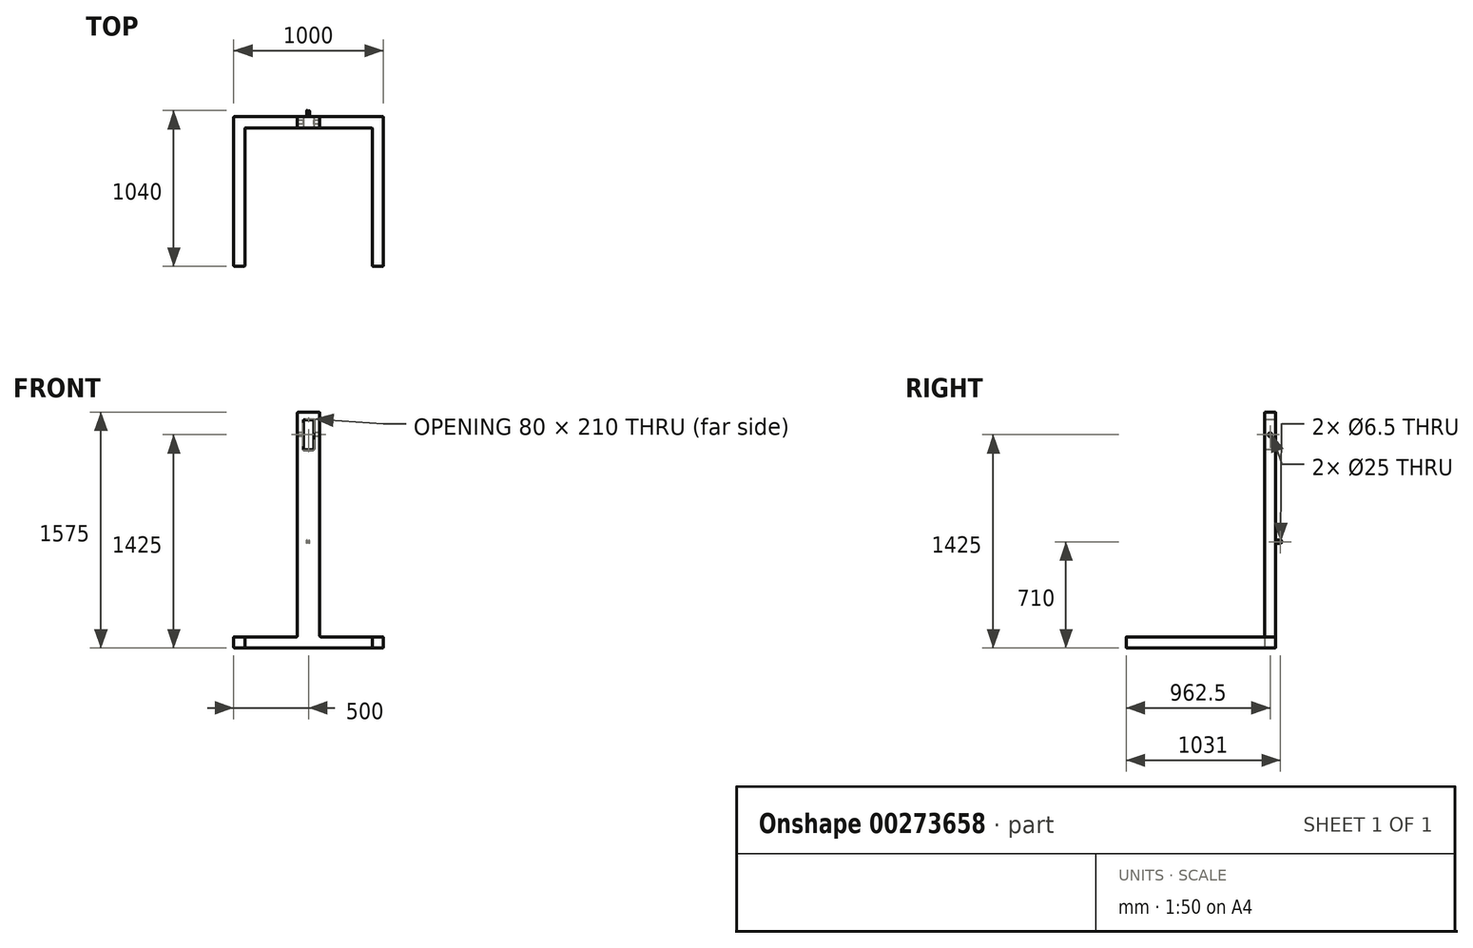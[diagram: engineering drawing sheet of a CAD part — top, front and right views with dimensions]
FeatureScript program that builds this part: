
annotation { "Feature Type Name" : "Feature", "Feature Type Description" : "" }
export const myFeature = defineFeature(function(context is Context, id is Id, definition is map)
    precondition{}
    {
        {
            var Q0;
            Q0=qCreatedBy(makeId("Top.planeOp"),FACE);
            var sketch = newSketch(context, id + "F0", { "sketchPlane" : qUnion([Q0])});
            skLineSegment(sketch, "E0.bottom", {"start": v(-500, 0) * mm, "end": v(500, 0) * mm});
            skLineSegment(sketch, "E0.top", {"start": v(-500, -1000) * mm, "end": v(-425, -1000) * mm});
            skLineSegment(sketch, "E0.left", {"start": v(-500, 0) * mm, "end": v(-500, -1000) * mm});
            skLineSegment(sketch, "E0.right", {"start": v(500, 0) * mm, "end": v(500, -1000) * mm});
            skLineSegment(sketch, "E1.0", {"start": v(-505, 5) * mm, "end": v(-505, -1000) * mm});
            skLineSegment(sketch, "E1.1", {"start": v(-505, 5) * mm, "end": v(505, 5) * mm});
            skLineSegment(sketch, "E1.2", {"start": v(505, 5) * mm, "end": v(505, -1000) * mm});
            skLineSegment(sketch, "E2.0", {"start": v(-425, -75) * mm, "end": v(-425, -1000) * mm});
            skLineSegment(sketch, "E2.1", {"start": v(-425, -75) * mm, "end": v(425, -75) * mm});
            skLineSegment(sketch, "E2.2", {"start": v(425, -75) * mm, "end": v(425, -1000) * mm});
            skLineSegment(sketch, "E3.trimOffspring", {"start": v(425, -1000) * mm, "end": v(500, -1000) * mm});
            skSolve(sketch);
        }
        {
            var Q0;
            Q0=makeQuery(id+"F0.imprint","IMPRINT",FACE,{"disambiguationData":[TD([[makeQuery(id+"F0.imprint","IMPRINT",EDGE,{"derivedFrom":sQuery(id+"F0.wireOp",EDGE,"E0.bottom")}),-1.0]])]});
            extrude(context, id + "F1", {"entities" : qUnion([Q0]), "depth" : 75 * mm});
        }
        {
            var Q0;
            Q0=makeQuery(id+"F1.opExtrude","CAP_FACE",FACE,{"disambiguationData":[OSD([sQuery(id+"F0.wireOp",EDGE,"E0.bottom"),sQuery(id+"F0.wireOp",EDGE,"E0.top"),sQuery(id+"F0.wireOp",EDGE,"E0.left"),sQuery(id+"F0.wireOp",EDGE,"E0.right"),sQuery(id+"F0.wireOp",EDGE,"E2.0"),sQuery(id+"F0.wireOp",EDGE,"E2.1"),sQuery(id+"F0.wireOp",EDGE,"E2.2"),sQuery(id+"F0.wireOp",EDGE,"E3.trimOffspring")])],"isStart":false});
            var sketch = newSketch(context, id + "F2", { "sketchPlane" : qUnion([Q0])});
            skLineSegment(sketch, "E4.bottom", {"start": v(75, -75) * mm, "end": v(-75, -75) * mm});
            skLineSegment(sketch, "E4.left", {"start": v(75, -75) * mm, "end": v(75, 0) * mm});
            skLineSegment(sketch, "E4.right", {"start": v(-75, -75) * mm, "end": v(-75, 0) * mm});
            skPoint(sketch, "E4.middle", {"position": v(0, 0) * mm});
            skLineSegment(sketch, "E5", {"start": v(-75, 0) * mm, "end": v(75, 0) * mm});
            skPoint(sketch, "E4.top.end.orphan", {"position": v(-75, 75) * mm});
            skPoint(sketch, "E6.orphan", {"position": v(75, 75) * mm});
            skSolve(sketch);
        }
        {
            var Q0;
            Q0=makeQuery(id+"F2.imprint","IMPRINT",FACE,{"disambiguationData":[TD([[makeQuery(id+"F2.imprint","IMPRINT",EDGE,{"derivedFrom":sQuery(id+"F2.wireOp",EDGE,"E4.bottom")}),1.0]])]});
            extrude(context, id + "F3", {"entities" : qUnion([Q0]), "operationType" : NewBodyOperationType.ADD, "depth" : 1500 * mm});
        }
        {
            var Q0;
            Q0=makeQuery(id+"F3.boolean.opBoolean","MERGE",FACE,{"derivedFrom":[makeQuery(id+"F1.opExtrude","SWEPT_FACE",FACE,{"disambiguationData":[OSD([sQuery(id+"F0.wireOp",EDGE,"E2.1")])]}),makeQuery(id+"F3.opExtrude","SWEPT_FACE",FACE,{"disambiguationData":[OSD([sQuery(id+"F2.wireOp",EDGE,"E4.bottom")])]})]});
            var sketch = newSketch(context, id + "F4", { "sketchPlane" : qUnion([Q0])});
            skLineSegment(sketch, "E7.bottom", {"start": v(-35, 1525) * mm, "end": v(35, 1525) * mm});
            skLineSegment(sketch, "E7.top", {"start": v(-35, 1325) * mm, "end": v(35, 1325) * mm});
            skLineSegment(sketch, "E7.left", {"start": v(-35, 1525) * mm, "end": v(-35, 1325) * mm});
            skLineSegment(sketch, "E7.right", {"start": v(35, 1525) * mm, "end": v(35, 1325) * mm});
            skSolve(sketch);
        }
        {
            var Q0;
            Q0=makeQuery(id+"F4.imprint","IMPRINT",FACE,{"disambiguationData":[TD([[makeQuery(id+"F4.imprint","IMPRINT",EDGE,{"derivedFrom":sQuery(id+"F4.wireOp",EDGE,"E7.bottom")}),-1.0]])]});
            extrude(context, id + "F5", {"entities" : qUnion([Q0]), "operationType" : NewBodyOperationType.REMOVE, "endBound" : BoundingType.THROUGH_ALL, "oppositeDirection" : true, "depth" : 25 * mm});
        }
        {
            var Q0;
            Q0=makeQuery(id+"F3.boolean.opBoolean","MERGE",FACE,{"derivedFrom":[makeQuery(id+"F1.opExtrude","SWEPT_FACE",FACE,{"disambiguationData":[OSD([sQuery(id+"F0.wireOp",EDGE,"E0.bottom")])]}),makeQuery(id+"F3.opExtrude","SWEPT_FACE",FACE,{"disambiguationData":[OSD([sQuery(id+"F2.wireOp",EDGE,"E5")])]})]});
            var sketch = newSketch(context, id + "F6", { "sketchPlane" : qUnion([Q0])});
            skLineSegment(sketch, "E8.bottom", {"start": v(-7.5, 700) * mm, "end": v(-1.5, 700) * mm});
            skLineSegment(sketch, "E8.top", {"start": v(-7.5, 720) * mm, "end": v(-1.5, 720) * mm});
            skLineSegment(sketch, "E8.left", {"start": v(-7.5, 700) * mm, "end": v(-7.5, 720) * mm});
            skLineSegment(sketch, "E8.right", {"start": v(-1.5, 700) * mm, "end": v(-1.5, 720) * mm});
            skLineSegment(sketch, "E9.1.0.0", {"start": v(7.5, 700) * mm, "end": v(13.5, 700) * mm});
            skLineSegment(sketch, "E9.1.0.1", {"start": v(7.5, 720) * mm, "end": v(13.5, 720) * mm});
            skLineSegment(sketch, "E9.1.0.2", {"start": v(7.5, 700) * mm, "end": v(7.5, 720) * mm});
            skLineSegment(sketch, "E9.1.0.3", {"start": v(13.5, 700) * mm, "end": v(13.5, 720) * mm});
            skLineSegment(sketch, "E9.direction1", {"start": v(-7.5, 700) * mm, "end": v(7.5, 700) * mm, "construction": true});
            skSolve(sketch);
        }
        {
            var Q0;
            Q0=makeQuery(id+"F6.imprint","IMPRINT",FACE,{"disambiguationData":[TD([[makeQuery(id+"F6.imprint","IMPRINT",EDGE,{"derivedFrom":sQuery(id+"F6.wireOp",EDGE,"E8.bottom")}),1.0]])]});
            var Q1;
            Q1=makeQuery(id+"F6.imprint","IMPRINT",FACE,{"disambiguationData":[TD([[makeQuery(id+"F6.imprint","IMPRINT",EDGE,{"derivedFrom":sQuery(id+"F6.wireOp",EDGE,"E9.1.0.0")}),1.0]])]});
            extrude(context, id + "F7", {"entities" : qUnion([Q0, Q1]), "operationType" : NewBodyOperationType.ADD, "depth" : 40 * mm});
        }
        {
            var Q0;
            Q0=makeQuery(id+"F7.opExtrude","CAP_EDGE",EDGE,{"disambiguationData":[OSD([sQuery(id+"F6.wireOp",EDGE,"E8.top")])],"isStart":false});
            var Q1;
            Q1=makeQuery(id+"F7.opExtrude","CAP_EDGE",EDGE,{"disambiguationData":[OSD([sQuery(id+"F6.wireOp",EDGE,"E8.bottom")])],"isStart":false});
            var Q2;
            Q2=makeQuery(id+"F7.opExtrude","CAP_EDGE",EDGE,{"disambiguationData":[OSD([sQuery(id+"F6.wireOp",EDGE,"E9.1.0.1")])],"isStart":false});
            var Q3;
            Q3=makeQuery(id+"F7.opExtrude","CAP_EDGE",EDGE,{"disambiguationData":[OSD([sQuery(id+"F6.wireOp",EDGE,"E9.1.0.0")])],"isStart":false});
            fillet(context, id + "F8", {"entities" : qUnion([Q0, Q1, Q2, Q3]), "radius" : 10 * mm, "tangentPropagation" : true, "allowEdgeOverflow" : false});
        }
        {
            var Q0;
            Q0=makeQuery(id+"F7.opExtrude","SWEPT_FACE",FACE,{"disambiguationData":[OSD([sQuery(id+"F6.wireOp",EDGE,"E8.left")])]});
            var sketch = newSketch(context, id + "F9", { "sketchPlane" : qUnion([Q0])});
            skCircle(sketch, "E10", {"center": v(31, 710) * mm, "radius": 3.25 * mm});
            skSolve(sketch);
        }
        {
            var Q0;
            Q0 = qSketchRegion(id + "F9", true);
            extrude(context, id + "F10", {"entities" : qUnion([Q0]), "operationType" : NewBodyOperationType.REMOVE, "endBound" : BoundingType.THROUGH_ALL, "oppositeDirection" : true, "depth" : 25 * mm});
        }
        {
            var Q0;
            Q0=makeQuery(id+"F3.boolean.opBoolean","MERGE",FACE,{"derivedFrom":[makeQuery(id+"F1.opExtrude","SWEPT_FACE",FACE,{"disambiguationData":[OSD([sQuery(id+"F0.wireOp",EDGE,"E2.1")])]}),makeQuery(id+"F3.opExtrude","SWEPT_FACE",FACE,{"disambiguationData":[OSD([sQuery(id+"F2.wireOp",EDGE,"E4.bottom")])]})]});
            var Q1;
            {var subQ0=sQuery(id+"F0.wireOp",EDGE,"E2.0");var subQ1=sQuery(id+"F0.wireOp",EDGE,"E0.left");var subQ2=sQuery(id+"F0.wireOp",EDGE,"E0.top");var subQ3=sQuery(id+"F0.wireOp",EDGE,"E0.bottom");var subQ4=sQuery(id+"F0.wireOp",EDGE,"E2.1");Q1=makeQuery(id+"F3.boolean.opBoolean","SPLIT",FACE,{"disambiguationData":[TD([makeQuery(id+"F1.opExtrude","SWEPT_FACE",FACE,{"disambiguationData":[OSD([subQ2])]})])],"derivedFrom":makeQuery(id+"F1.opExtrude","CAP_FACE",FACE,{"disambiguationData":[OSD([subQ3,subQ2,subQ1,sQuery(id+"F0.wireOp",EDGE,"E0.right"),subQ0,subQ4,sQuery(id+"F0.wireOp",EDGE,"E2.2"),sQuery(id+"F0.wireOp",EDGE,"E3.trimOffspring")])],"isStart":false})});}
            var Q2;
            {var subQ0=sQuery(id+"F0.wireOp",EDGE,"E2.2");var subQ1=sQuery(id+"F0.wireOp",EDGE,"E2.1");var subQ2=sQuery(id+"F0.wireOp",EDGE,"E0.right");var subQ3=sQuery(id+"F0.wireOp",EDGE,"E0.bottom");var subQ4=sQuery(id+"F0.wireOp",EDGE,"E3.trimOffspring");Q2=makeQuery(id+"F3.boolean.opBoolean","SPLIT",FACE,{"disambiguationData":[TD([makeQuery(id+"F1.opExtrude","SWEPT_FACE",FACE,{"disambiguationData":[OSD([subQ2])]})])],"derivedFrom":makeQuery(id+"F1.opExtrude","CAP_FACE",FACE,{"disambiguationData":[OSD([subQ3,sQuery(id+"F0.wireOp",EDGE,"E0.top"),sQuery(id+"F0.wireOp",EDGE,"E0.left"),subQ2,sQuery(id+"F0.wireOp",EDGE,"E2.0"),subQ1,subQ0,subQ4])],"isStart":false})});}
            var Q3;
            Q3=makeQuery(id+"F1.opExtrude","SWEPT_FACE",FACE,{"disambiguationData":[OSD([sQuery(id+"F0.wireOp",EDGE,"E0.top")])]});
            var Q4;
            Q4=makeQuery(id+"F1.opExtrude","SWEPT_FACE",FACE,{"disambiguationData":[OSD([sQuery(id+"F0.wireOp",EDGE,"E3.trimOffspring")])]});
            var Q5;
            Q5=makeQuery(id+"F1.opExtrude","SWEPT_FACE",FACE,{"disambiguationData":[OSD([sQuery(id+"F0.wireOp",EDGE,"E0.left")])]});
            var Q6;
            Q6=makeQuery(id+"F1.opExtrude","SWEPT_EDGE",EDGE,{"disambiguationData":[OSD([sQuery(id+"F0.wireOp",EDGE,"E0.top"),sQuery(id+"F0.wireOp",EDGE,"E0.left")])]});
            var Q7;
            Q7=makeQuery(id+"F3.opExtrude","SWEPT_EDGE",EDGE,{"disambiguationData":[OSD([sQuery(id+"F0.wireOp",EDGE,"E2.1"),sQuery(id+"F2.wireOp",EDGE,"E4.bottom"),sQuery(id+"F2.wireOp",EDGE,"E4.left")])]});
            var Q8;
            Q8=makeQuery(id+"F1.opExtrude","SWEPT_EDGE",EDGE,{"disambiguationData":[OSD([sQuery(id+"F0.wireOp",EDGE,"E2.2"),sQuery(id+"F0.wireOp",EDGE,"E3.trimOffspring")])]});
            var Q9;
            Q9=makeQuery(id+"F3.opExtrude","SWEPT_EDGE",EDGE,{"disambiguationData":[OSD([sQuery(id+"F0.wireOp",EDGE,"E2.1"),sQuery(id+"F2.wireOp",EDGE,"E4.bottom"),sQuery(id+"F2.wireOp",EDGE,"E4.right")])]});
            var Q10;
            Q10=makeQuery(id+"F5.boolean.opBoolean","COPY",EDGE,{"derivedFrom":makeQuery(id+"F5.opExtrude","CAP_EDGE",EDGE,{"disambiguationData":[OSD([sQuery(id+"F4.wireOp",EDGE,"E7.right")])],"isStart":true})});
            var Q11;
            Q11=makeQuery(id+"F1.opExtrude","SWEPT_EDGE",EDGE,{"disambiguationData":[OSD([sQuery(id+"F0.wireOp",EDGE,"E0.top"),sQuery(id+"F0.wireOp",EDGE,"E2.0")])]});
            var Q12;
            Q12=makeQuery(id+"F1.opExtrude","SWEPT_EDGE",EDGE,{"disambiguationData":[OSD([sQuery(id+"F0.wireOp",EDGE,"E2.1"),sQuery(id+"F0.wireOp",EDGE,"E2.2")])]});
            var Q13;
            Q13=makeQuery(id+"F3.opExtrude","SWEPT_EDGE",EDGE,{"disambiguationData":[OSD([sQuery(id+"F0.wireOp",EDGE,"E0.bottom"),sQuery(id+"F2.wireOp",EDGE,"E4.left"),sQuery(id+"F2.wireOp",EDGE,"E5")])]});
            var Q14;
            Q14=makeQuery(id+"F1.opExtrude","SWEPT_EDGE",EDGE,{"disambiguationData":[OSD([sQuery(id+"F0.wireOp",EDGE,"E2.0"),sQuery(id+"F0.wireOp",EDGE,"E2.1")])]});
            var Q15;
            Q15=makeQuery(id+"F1.opExtrude","SWEPT_EDGE",EDGE,{"disambiguationData":[OSD([sQuery(id+"F0.wireOp",EDGE,"E0.bottom"),sQuery(id+"F0.wireOp",EDGE,"E0.left")])]});
            var Q16;
            Q16=makeQuery(id+"F1.opExtrude","CAP_EDGE",EDGE,{"disambiguationData":[OSD([sQuery(id+"F0.wireOp",EDGE,"E0.right")])],"isStart":false});
            var Q17;
            Q17=makeQuery(id+"F1.opExtrude","CAP_EDGE",EDGE,{"disambiguationData":[OSD([sQuery(id+"F0.wireOp",EDGE,"E0.right")])],"isStart":true});
            var Q18;
            Q18=makeQuery(id+"F1.opExtrude","CAP_EDGE",EDGE,{"disambiguationData":[OSD([sQuery(id+"F0.wireOp",EDGE,"E0.left")])],"isStart":false});
            var Q19;
            Q19=makeQuery(id+"F1.opExtrude","CAP_EDGE",EDGE,{"disambiguationData":[OSD([sQuery(id+"F0.wireOp",EDGE,"E0.top")])],"isStart":true});
            var Q20;
            Q20=makeQuery(id+"F1.opExtrude","CAP_EDGE",EDGE,{"disambiguationData":[OSD([sQuery(id+"F0.wireOp",EDGE,"E0.left")])],"isStart":true});
            var Q21;
            Q21=makeQuery(id+"F1.opExtrude","CAP_EDGE",EDGE,{"disambiguationData":[OSD([sQuery(id+"F0.wireOp",EDGE,"E2.0")])],"isStart":true});
            var Q22;
            Q22=makeQuery(id+"F1.opExtrude","CAP_EDGE",EDGE,{"disambiguationData":[OSD([sQuery(id+"F0.wireOp",EDGE,"E2.0")])],"isStart":false});
            var Q23;
            Q23=makeQuery(id+"F1.opExtrude","CAP_EDGE",EDGE,{"disambiguationData":[OSD([sQuery(id+"F0.wireOp",EDGE,"E2.2")])],"isStart":true});
            var Q24;
            Q24=makeQuery(id+"F1.opExtrude","CAP_EDGE",EDGE,{"disambiguationData":[OSD([sQuery(id+"F0.wireOp",EDGE,"E2.2")])],"isStart":false});
            var Q25;
            Q25=makeQuery(id+"F3.opExtrude","SWEPT_EDGE",EDGE,{"disambiguationData":[OSD([sQuery(id+"F0.wireOp",EDGE,"E0.bottom"),sQuery(id+"F2.wireOp",EDGE,"E4.right"),sQuery(id+"F2.wireOp",EDGE,"E5")])]});
            var Q26;
            Q26=makeQuery(id+"F3.opExtrude","CAP_EDGE",EDGE,{"disambiguationData":[OSD([sQuery(id+"F2.wireOp",EDGE,"E4.bottom")])],"isStart":false});
            var Q27;
            Q27=makeQuery(id+"F3.opExtrude","CAP_EDGE",EDGE,{"disambiguationData":[OSD([sQuery(id+"F2.wireOp",EDGE,"E4.right")])],"isStart":false});
            var Q28;
            Q28=makeQuery(id+"F3.opExtrude","CAP_EDGE",EDGE,{"disambiguationData":[OSD([sQuery(id+"F2.wireOp",EDGE,"E4.right")])],"isStart":true});
            var Q29;
            {var subQ0=sQuery(id+"F0.wireOp",EDGE,"E2.1");var subQ1=sQuery(id+"F0.wireOp",EDGE,"E2.2");Q29=makeQuery(id+"F3.boolean.opBoolean","SPLIT",EDGE,{"disambiguationData":[TD([makeQuery(id+"F1.opExtrude","SWEPT_FACE",FACE,{"disambiguationData":[OSD([subQ1])]})])],"derivedFrom":makeQuery(id+"F1.opExtrude","CAP_EDGE",EDGE,{"disambiguationData":[OSD([subQ0])],"isStart":false})});}
            var Q30;
            Q30=makeQuery(id+"F5.boolean.opBoolean","COPY",EDGE,{"derivedFrom":makeQuery(id+"F5.opExtrude","SWEPT_EDGE",EDGE,{"disambiguationData":[OSD([sQuery(id+"F4.wireOp",EDGE,"E7.top"),sQuery(id+"F4.wireOp",EDGE,"E7.left")])]})});
            var Q31;
            Q31=makeQuery(id+"F7.opExtrude","CAP_EDGE",EDGE,{"disambiguationData":[OSD([sQuery(id+"F6.wireOp",EDGE,"E8.top")])],"isStart":true});
            var Q32;
            Q32=makeQuery(id+"F8.opFillet","BLEND_EDGE",EDGE,{"blendedFrom":[makeQuery(id+"F7.opExtrude","CAP_EDGE",EDGE,{"disambiguationData":[OSD([sQuery(id+"F6.wireOp",EDGE,"E8.top")])],"isStart":false}),makeQuery(id+"F7.opExtrude","SWEPT_FACE",FACE,{"disambiguationData":[OSD([sQuery(id+"F6.wireOp",EDGE,"E8.right")])]})],"blendedInto":[makeQuery(id+"F7.opExtrude","SWEPT_FACE",FACE,{"disambiguationData":[OSD([sQuery(id+"F6.wireOp",EDGE,"E8.right")])]})]});
            var Q33;
            Q33=makeQuery(id+"F7.opExtrude","CAP_EDGE",EDGE,{"disambiguationData":[OSD([sQuery(id+"F6.wireOp",EDGE,"E8.bottom")])],"isStart":true});
            var Q34;
            Q34=makeQuery(id+"F7.opExtrude","CAP_EDGE",EDGE,{"disambiguationData":[OSD([sQuery(id+"F6.wireOp",EDGE,"E8.right")])],"isStart":true});
            var Q35;
            Q35=makeQuery(id+"F1.opExtrude","SWEPT_EDGE",EDGE,{"disambiguationData":[OSD([sQuery(id+"F0.wireOp",EDGE,"E0.bottom"),sQuery(id+"F0.wireOp",EDGE,"E0.right")])]});
            var Q36;
            Q36=makeQuery(id+"F1.opExtrude","CAP_EDGE",EDGE,{"disambiguationData":[OSD([sQuery(id+"F0.wireOp",EDGE,"E0.bottom")])],"isStart":true});
            var Q37;
            Q37=makeQuery(id+"F1.opExtrude","SWEPT_EDGE",EDGE,{"disambiguationData":[OSD([sQuery(id+"F0.wireOp",EDGE,"E0.right"),sQuery(id+"F0.wireOp",EDGE,"E3.trimOffspring")])]});
            var Q38;
            Q38=makeQuery(id+"F1.opExtrude","CAP_EDGE",EDGE,{"disambiguationData":[OSD([sQuery(id+"F0.wireOp",EDGE,"E0.top")])],"isStart":false});
            var Q39;
            Q39=makeQuery(id+"F1.opExtrude","CAP_EDGE",EDGE,{"disambiguationData":[OSD([sQuery(id+"F0.wireOp",EDGE,"E2.1")])],"isStart":true});
            var Q40;
            Q40=makeQuery(id+"F1.opExtrude","CAP_EDGE",EDGE,{"disambiguationData":[OSD([sQuery(id+"F0.wireOp",EDGE,"E3.trimOffspring")])],"isStart":true});
            var Q41;
            Q41=makeQuery(id+"F1.opExtrude","CAP_EDGE",EDGE,{"disambiguationData":[OSD([sQuery(id+"F0.wireOp",EDGE,"E3.trimOffspring")])],"isStart":false});
            var Q42;
            Q42=makeQuery(id+"F3.opExtrude","CAP_EDGE",EDGE,{"disambiguationData":[OSD([sQuery(id+"F2.wireOp",EDGE,"E4.left")])],"isStart":false});
            var Q43;
            Q43=makeQuery(id+"F3.opExtrude","CAP_EDGE",EDGE,{"disambiguationData":[OSD([sQuery(id+"F2.wireOp",EDGE,"E5")])],"isStart":false});
            var Q44;
            Q44=makeQuery(id+"F3.opExtrude","CAP_EDGE",EDGE,{"disambiguationData":[OSD([sQuery(id+"F2.wireOp",EDGE,"E4.left")])],"isStart":true});
            var Q45;
            Q45=makeQuery(id+"F5.boolean.opBoolean","COPY",EDGE,{"derivedFrom":makeQuery(id+"F5.opExtrude","SWEPT_EDGE",EDGE,{"disambiguationData":[OSD([sQuery(id+"F4.wireOp",EDGE,"E7.bottom"),sQuery(id+"F4.wireOp",EDGE,"E7.left")])]})});
            var Q46;
            {var subQ0=sQuery(id+"F0.wireOp",EDGE,"E0.left");var subQ1=sQuery(id+"F0.wireOp",EDGE,"E0.bottom");Q46=makeQuery(id+"F3.boolean.opBoolean","SPLIT",EDGE,{"disambiguationData":[TD([makeQuery(id+"F1.opExtrude","SWEPT_FACE",FACE,{"disambiguationData":[OSD([subQ0])]})])],"derivedFrom":makeQuery(id+"F1.opExtrude","CAP_EDGE",EDGE,{"disambiguationData":[OSD([subQ1])],"isStart":false})});}
            var Q47;
            {var subQ0=sQuery(id+"F0.wireOp",EDGE,"E2.1");var subQ1=sQuery(id+"F0.wireOp",EDGE,"E2.0");Q47=makeQuery(id+"F3.boolean.opBoolean","SPLIT",EDGE,{"disambiguationData":[TD([makeQuery(id+"F1.opExtrude","SWEPT_FACE",FACE,{"disambiguationData":[OSD([subQ1])]})])],"derivedFrom":makeQuery(id+"F1.opExtrude","CAP_EDGE",EDGE,{"disambiguationData":[OSD([subQ0])],"isStart":false})});}
            var Q48;
            Q48=makeQuery(id+"F5.boolean.opBoolean","COPY",EDGE,{"derivedFrom":makeQuery(id+"F5.opExtrude","SWEPT_EDGE",EDGE,{"disambiguationData":[OSD([sQuery(id+"F4.wireOp",EDGE,"E7.top"),sQuery(id+"F4.wireOp",EDGE,"E7.right")])]})});
            var Q49;
            Q49=makeQuery(id+"F5.boolean.opBoolean","COPY",EDGE,{"derivedFrom":makeQuery(id+"F5.opExtrude","CAP_EDGE",EDGE,{"disambiguationData":[OSD([sQuery(id+"F4.wireOp",EDGE,"E7.top")])],"isStart":true})});
            var Q50;
            Q50=makeQuery(id+"F5.boolean.opBoolean","COPY",EDGE,{"derivedFrom":makeQuery(id+"F5.opExtrude","CAP_EDGE",EDGE,{"disambiguationData":[OSD([sQuery(id+"F4.wireOp",EDGE,"E7.left")])],"isStart":true})});
            var Q51;
            Q51=makeQuery(id+"F5.boolean.opBoolean","INTERSECT",EDGE,{"derivedFrom":[makeQuery(id+"F3.boolean.opBoolean","MERGE",FACE,{"derivedFrom":[makeQuery(id+"F1.opExtrude","SWEPT_FACE",FACE,{"disambiguationData":[OSD([sQuery(id+"F0.wireOp",EDGE,"E0.bottom")])]}),makeQuery(id+"F3.opExtrude","SWEPT_FACE",FACE,{"disambiguationData":[OSD([sQuery(id+"F2.wireOp",EDGE,"E5")])]})]}),makeQuery(id+"F5.opExtrude","SWEPT_FACE",FACE,{"disambiguationData":[OSD([sQuery(id+"F4.wireOp",EDGE,"E7.top")])]})]});
            var Q52;
            Q52=makeQuery(id+"F5.boolean.opBoolean","INTERSECT",EDGE,{"derivedFrom":[makeQuery(id+"F3.boolean.opBoolean","MERGE",FACE,{"derivedFrom":[makeQuery(id+"F1.opExtrude","SWEPT_FACE",FACE,{"disambiguationData":[OSD([sQuery(id+"F0.wireOp",EDGE,"E0.bottom")])]}),makeQuery(id+"F3.opExtrude","SWEPT_FACE",FACE,{"disambiguationData":[OSD([sQuery(id+"F2.wireOp",EDGE,"E5")])]})]}),makeQuery(id+"F5.opExtrude","SWEPT_FACE",FACE,{"disambiguationData":[OSD([sQuery(id+"F4.wireOp",EDGE,"E7.left")])]})]});
            var Q53;
            Q53=makeQuery(id+"F5.boolean.opBoolean","INTERSECT",EDGE,{"derivedFrom":[makeQuery(id+"F3.boolean.opBoolean","MERGE",FACE,{"derivedFrom":[makeQuery(id+"F1.opExtrude","SWEPT_FACE",FACE,{"disambiguationData":[OSD([sQuery(id+"F0.wireOp",EDGE,"E0.bottom")])]}),makeQuery(id+"F3.opExtrude","SWEPT_FACE",FACE,{"disambiguationData":[OSD([sQuery(id+"F2.wireOp",EDGE,"E5")])]})]}),makeQuery(id+"F5.opExtrude","SWEPT_FACE",FACE,{"disambiguationData":[OSD([sQuery(id+"F4.wireOp",EDGE,"E7.right")])]})]});
            var Q54;
            Q54=makeQuery(id+"F7.opExtrude","CAP_EDGE",EDGE,{"disambiguationData":[OSD([sQuery(id+"F6.wireOp",EDGE,"E8.left")])],"isStart":true});
            var Q55;
            Q55=makeQuery(id+"F8.opFillet","BLEND_EDGE",EDGE,{"blendedFrom":[makeQuery(id+"F7.opExtrude","CAP_EDGE",EDGE,{"disambiguationData":[OSD([sQuery(id+"F6.wireOp",EDGE,"E8.top")])],"isStart":false}),makeQuery(id+"F7.opExtrude","SWEPT_FACE",FACE,{"disambiguationData":[OSD([sQuery(id+"F6.wireOp",EDGE,"E8.left")])]})],"blendedInto":[makeQuery(id+"F7.opExtrude","SWEPT_FACE",FACE,{"disambiguationData":[OSD([sQuery(id+"F6.wireOp",EDGE,"E8.left")])]})]});
            var Q56;
            Q56=makeQuery(id+"F7.opExtrude","SWEPT_EDGE",EDGE,{"disambiguationData":[OSD([sQuery(id+"F6.wireOp",EDGE,"E8.top"),sQuery(id+"F6.wireOp",EDGE,"E8.right")])]});
            var Q57;
            Q57=makeQuery(id+"F7.opExtrude","SWEPT_EDGE",EDGE,{"disambiguationData":[OSD([sQuery(id+"F6.wireOp",EDGE,"E8.bottom"),sQuery(id+"F6.wireOp",EDGE,"E8.right")])]});
            var Q58;
            {var subQ0=sQuery(id+"F0.wireOp",EDGE,"E0.right");var subQ1=sQuery(id+"F0.wireOp",EDGE,"E0.bottom");Q58=makeQuery(id+"F3.boolean.opBoolean","SPLIT",EDGE,{"disambiguationData":[TD([makeQuery(id+"F1.opExtrude","SWEPT_FACE",FACE,{"disambiguationData":[OSD([subQ0])]})])],"derivedFrom":makeQuery(id+"F1.opExtrude","CAP_EDGE",EDGE,{"disambiguationData":[OSD([subQ1])],"isStart":false})});}
            var Q59;
            Q59=makeQuery(id+"F5.boolean.opBoolean","COPY",EDGE,{"derivedFrom":makeQuery(id+"F5.opExtrude","SWEPT_EDGE",EDGE,{"disambiguationData":[OSD([sQuery(id+"F4.wireOp",EDGE,"E7.bottom"),sQuery(id+"F4.wireOp",EDGE,"E7.right")])]})});
            var Q60;
            Q60=makeQuery(id+"F5.boolean.opBoolean","COPY",EDGE,{"derivedFrom":makeQuery(id+"F5.opExtrude","CAP_EDGE",EDGE,{"disambiguationData":[OSD([sQuery(id+"F4.wireOp",EDGE,"E7.bottom")])],"isStart":true})});
            var Q61;
            Q61=makeQuery(id+"F5.boolean.opBoolean","INTERSECT",EDGE,{"derivedFrom":[makeQuery(id+"F3.boolean.opBoolean","MERGE",FACE,{"derivedFrom":[makeQuery(id+"F1.opExtrude","SWEPT_FACE",FACE,{"disambiguationData":[OSD([sQuery(id+"F0.wireOp",EDGE,"E0.bottom")])]}),makeQuery(id+"F3.opExtrude","SWEPT_FACE",FACE,{"disambiguationData":[OSD([sQuery(id+"F2.wireOp",EDGE,"E5")])]})]}),makeQuery(id+"F5.opExtrude","SWEPT_FACE",FACE,{"disambiguationData":[OSD([sQuery(id+"F4.wireOp",EDGE,"E7.bottom")])]})]});
            var Q62;
            Q62=makeQuery(id+"F7.opExtrude","SWEPT_EDGE",EDGE,{"disambiguationData":[OSD([sQuery(id+"F6.wireOp",EDGE,"E8.bottom"),sQuery(id+"F6.wireOp",EDGE,"E8.left")])]});
            var Q63;
            Q63=makeQuery(id+"F7.opExtrude","SWEPT_EDGE",EDGE,{"disambiguationData":[OSD([sQuery(id+"F6.wireOp",EDGE,"E8.top"),sQuery(id+"F6.wireOp",EDGE,"E8.left")])]});
            var Q64;
            {var subQ0=sQuery(id+"F6.wireOp",EDGE,"E8.bottom");Q64=makeQuery(id+"F8.opFillet","BLEND_EDGE",EDGE,{"blendedFrom":[makeQuery(id+"F7.opExtrude","CAP_EDGE",EDGE,{"disambiguationData":[OSD([subQ0])],"isStart":false}),makeQuery(id+"F7.opExtrude","SWEPT_FACE",FACE,{"disambiguationData":[OSD([subQ0])]})],"blendedInto":[makeQuery(id+"F7.opExtrude","SWEPT_FACE",FACE,{"disambiguationData":[OSD([subQ0])]})]});}
            var Q65;
            {var subQ0=sQuery(id+"F6.wireOp",EDGE,"E8.top");Q65=makeQuery(id+"F8.opFillet","BLEND_EDGE",EDGE,{"blendedFrom":[makeQuery(id+"F7.opExtrude","CAP_EDGE",EDGE,{"disambiguationData":[OSD([subQ0])],"isStart":false}),makeQuery(id+"F7.opExtrude","SWEPT_FACE",FACE,{"disambiguationData":[OSD([subQ0])]})],"blendedInto":[makeQuery(id+"F7.opExtrude","SWEPT_FACE",FACE,{"disambiguationData":[OSD([subQ0])]})]});}
            fillet(context, id + "F11", {"entities" : qUnion([Q0, Q1, Q2, Q3, Q4, Q5, Q6, Q7, Q8, Q9, Q10, Q11, Q12, Q13, Q14, Q15, Q16, Q17, Q18, Q19, Q20, Q21, Q22, Q23, Q24, Q25, Q26, Q27, Q28, Q29, Q30, Q31, Q32, Q33, Q34, Q35, Q36, Q37, Q38, Q39, Q40, Q41, Q42, Q43, Q44, Q45, Q46, Q47, Q48, Q49, Q50, Q51, Q52, Q53, Q54, Q55, Q56, Q57, Q58, Q59, Q60, Q61, Q62, Q63, Q64, Q65]), "radius" : 5 * mm, "tangentPropagation" : true, "allowEdgeOverflow" : false});
        }
        {
            var Q0;
            Q0=makeQuery(id+"F3.opExtrude","SWEPT_FACE",FACE,{"disambiguationData":[OSD([sQuery(id+"F2.wireOp",EDGE,"E4.right")])]});
            var sketch = newSketch(context, id + "F12", { "sketchPlane" : qUnion([Q0])});
            skCircle(sketch, "E11", {"center": v(37.5, 1425) * mm, "radius": 12.5 * mm});
            skSolve(sketch);
        }
        {
            var Q0;
            Q0 = qSketchRegion(id + "F12", true);
            extrude(context, id + "F13", {"entities" : qUnion([Q0]), "operationType" : NewBodyOperationType.REMOVE, "endBound" : BoundingType.THROUGH_ALL, "oppositeDirection" : true, "depth" : 25 * mm});
        }
    });
